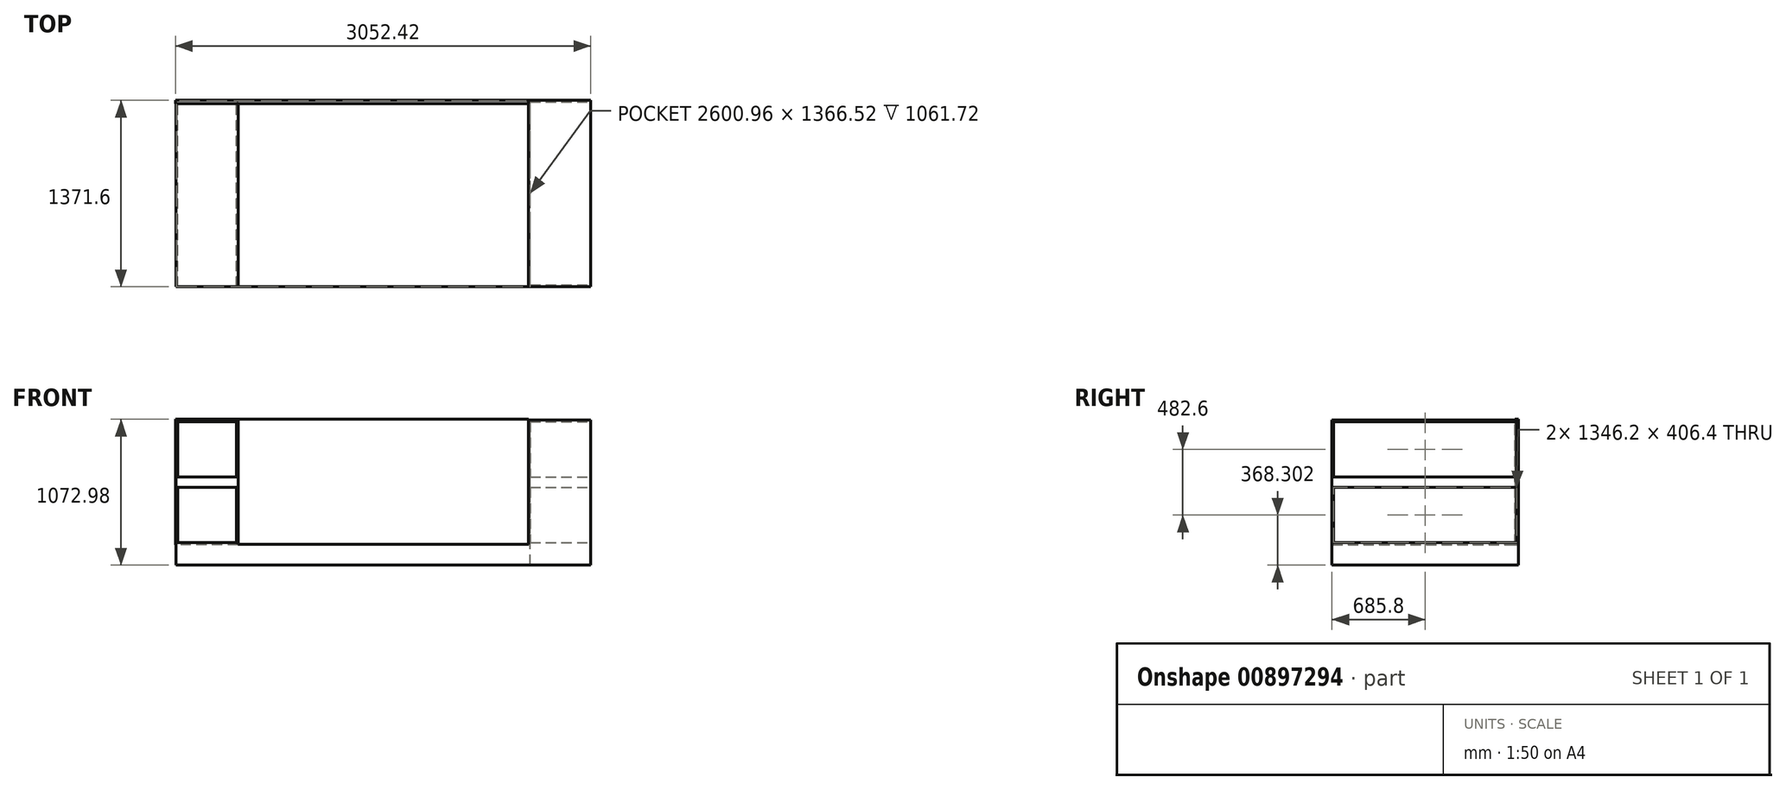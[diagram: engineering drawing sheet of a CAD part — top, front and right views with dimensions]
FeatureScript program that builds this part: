
annotation { "Feature Type Name" : "Feature", "Feature Type Description" : "" }
export const myFeature = defineFeature(function(context is Context, id is Id, definition is map)
    precondition{}
    {
        {
            var Q0;
            Q0=qCreatedBy(makeId("Front.planeOp"),FACE);
            var sketch = newSketch(context, id + "F0", { "sketchPlane" : qUnion([Q0])});
            skLineSegment(sketch, "E0.bottom", {"start": v(-2578.1, 79.5) * mm, "end": v(-444.5, 79.5) * mm});
            skLineSegment(sketch, "E0.top", {"start": v(-3035.3, -72.9) * mm, "end": v(12.7, -72.9) * mm});
            skLineSegment(sketch, "E0.left", {"start": v(-3035.3, 79.5) * mm, "end": v(-3035.3, -72.9) * mm});
            skLineSegment(sketch, "E0.right", {"start": v(12.7, 79.5) * mm, "end": v(12.7, -72.9) * mm});
            skLineSegment(sketch, "E1.top", {"start": v(-3035.3, 993.9) * mm, "end": v(-2578.1, 993.9) * mm});
            skLineSegment(sketch, "E1.left", {"start": v(-3035.3, 79.5) * mm, "end": v(-3035.3, 993.9) * mm});
            skLineSegment(sketch, "E1.right", {"start": v(-2578.1, 79.5) * mm, "end": v(-2578.1, 993.9) * mm});
            skLineSegment(sketch, "E2.top", {"start": v(12.7, 993.9) * mm, "end": v(-444.5, 993.9) * mm});
            skLineSegment(sketch, "E2.left", {"start": v(12.7, 79.5) * mm, "end": v(12.7, 993.9) * mm});
            skLineSegment(sketch, "E2.right", {"start": v(-444.5, 79.5) * mm, "end": v(-444.5, 993.9) * mm});
            skLineSegment(sketch, "E3.bottom", {"start": v(-3022.6, 498.6) * mm, "end": v(-2590.8, 498.6) * mm});
            skLineSegment(sketch, "E3.top", {"start": v(-3022.6, 92.2) * mm, "end": v(-2590.8, 92.2) * mm});
            skLineSegment(sketch, "E3.left", {"start": v(-3022.6, 498.6) * mm, "end": v(-3022.6, 92.2) * mm});
            skLineSegment(sketch, "E3.right", {"start": v(-2590.8, 498.6) * mm, "end": v(-2590.8, 92.2) * mm});
            skLineSegment(sketch, "E4.bottom", {"start": v(-3022.6, 981.2) * mm, "end": v(-2590.8, 981.2) * mm});
            skLineSegment(sketch, "E4.top", {"start": v(-3022.6, 574.8) * mm, "end": v(-2590.8, 574.8) * mm});
            skLineSegment(sketch, "E4.left", {"start": v(-3022.6, 981.2) * mm, "end": v(-3022.6, 574.8) * mm});
            skLineSegment(sketch, "E4.right", {"start": v(-2590.8, 981.2) * mm, "end": v(-2590.8, 574.8) * mm});
            skSolve(sketch);
        }
        {
            var Q0;
            Q0 = qSketchRegion(id + "F0", true);
            extrude(context, id + "F1", {"entities" : qUnion([Q0]), "depth" : 1371.6 * mm, "offsetDistance" : 25.4 * mm});
        }
        {
            var Q0;
            Q0=makeQuery(id+"F1.opExtrude","SWEPT_FACE",FACE,{"disambiguationData":[OSD([sQuery(id+"F0.wireOp",EDGE,"E0.right"),sQuery(id+"F0.wireOp",EDGE,"E2.left")])]});
            var sketch = newSketch(context, id + "F2", { "sketchPlane" : qUnion([Q0])});
            skLineSegment(sketch, "E5.bottom", {"start": v(-1358.9, 981.2) * mm, "end": v(-12.7, 981.2) * mm});
            skLineSegment(sketch, "E5.top", {"start": v(-1358.9, 574.8) * mm, "end": v(-12.7, 574.8) * mm});
            skLineSegment(sketch, "E5.left", {"start": v(-1358.9, 981.2) * mm, "end": v(-1358.9, 574.8) * mm});
            skLineSegment(sketch, "E5.right", {"start": v(-12.7, 981.2) * mm, "end": v(-12.7, 574.8) * mm});
            skLineSegment(sketch, "E6.bottom", {"start": v(-1358.9, 498.6) * mm, "end": v(-12.7, 498.6) * mm});
            skLineSegment(sketch, "E6.top", {"start": v(-1358.9, 92.2) * mm, "end": v(-12.7, 92.2) * mm});
            skLineSegment(sketch, "E6.left", {"start": v(-1358.9, 498.6) * mm, "end": v(-1358.9, 92.2) * mm});
            skLineSegment(sketch, "E6.right", {"start": v(-12.7, 498.6) * mm, "end": v(-12.7, 92.2) * mm});
            skSolve(sketch);
        }
        {
            var Q0;
            Q0=makeQuery(id+"F1.opExtrude","SWEPT_FACE",FACE,{"disambiguationData":[OSD([sQuery(id+"F0.wireOp",EDGE,"E0.right"),sQuery(id+"F0.wireOp",EDGE,"E2.left")])]});
            shell(context, id + "F3", {"entities" : qUnion([Q0]), "thickness" : 2.54 * mm});
        }
        {
            var Q0;
            Q0=makeQuery(id+"F2.imprint","IMPRINT",FACE,{"disambiguationData":[TD([[makeQuery(id+"F2.imprint","IMPRINT",EDGE,{"derivedFrom":sQuery(id+"F2.wireOp",EDGE,"E5.bottom")}),1.0]])]});
            extrude(context, id + "F4", {"entities" : qUnion([Q0]), "operationType" : NewBodyOperationType.ADD, "oppositeDirection" : true, "depth" : 444.5 * mm, "offsetDistance" : 25.4 * mm});
        }
        {
            var Q0;
            Q0=qCreatedBy(makeId("Front.planeOp"),FACE);
            var sketch = newSketch(context, id + "F5", { "sketchPlane" : qUnion([Q0])});
            skLineSegment(sketch, "E7.bottom", {"start": v(-3039.72, 1000.07) * mm, "end": v(-445.44, 1000.07) * mm});
            skLineSegment(sketch, "E7.top", {"start": v(-3039.72, 78.1) * mm, "end": v(-445.44, 78.1) * mm});
            skLineSegment(sketch, "E7.left", {"start": v(-3039.72, 1000.07) * mm, "end": v(-3039.72, 78.1) * mm});
            skLineSegment(sketch, "E7.right", {"start": v(-445.44, 1000.07) * mm, "end": v(-445.44, 78.1) * mm});
            skSolve(sketch);
        }
        {
            var Q0;
            Q0=makeQuery(id+"F5.imprint","IMPRINT",FACE,{"disambiguationData":[TD([[makeQuery(id+"F5.imprint","IMPRINT",EDGE,{"derivedFrom":sQuery(id+"F5.wireOp",EDGE,"E7.bottom")}),-1.0]])]});
            extrude(context, id + "F6", {"entities" : qUnion([Q0]), "operationType" : NewBodyOperationType.ADD, "depth" : 25.4 * mm, "offsetDistance" : 25.4 * mm});
        }
    });
